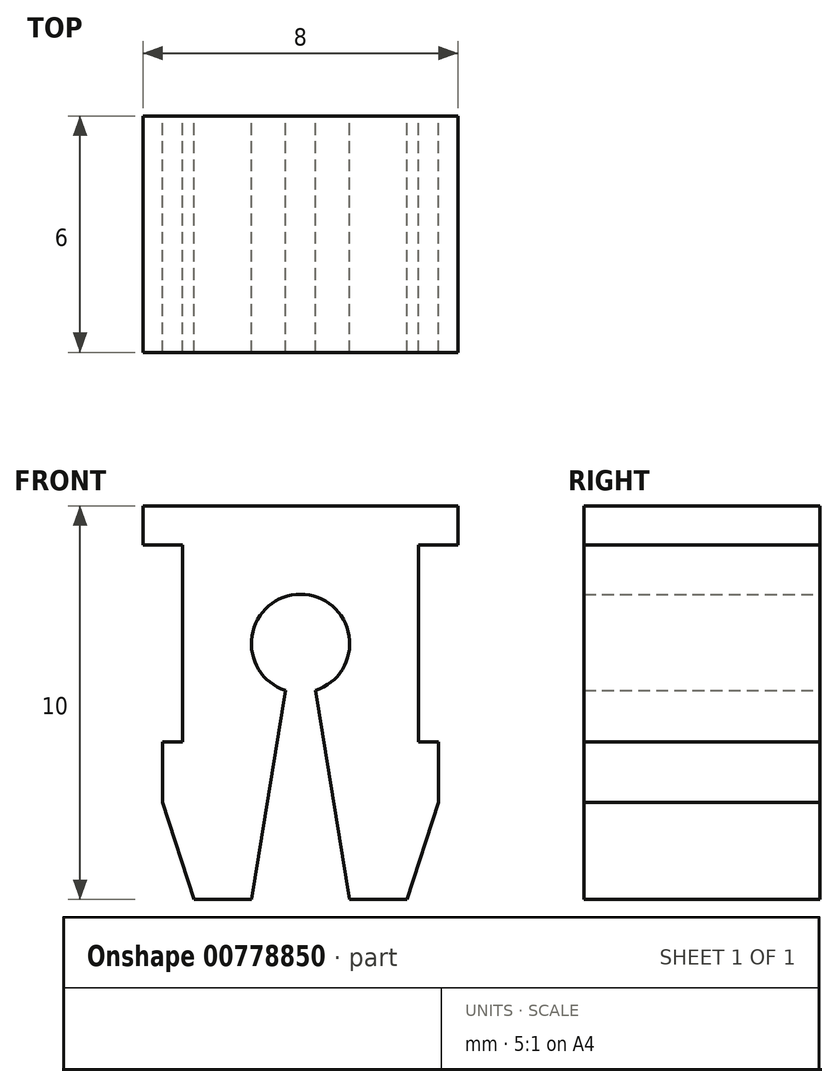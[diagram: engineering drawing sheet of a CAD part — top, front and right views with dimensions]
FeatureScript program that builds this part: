
annotation { "Feature Type Name" : "Feature", "Feature Type Description" : "" }
export const myFeature = defineFeature(function(context is Context, id is Id, definition is map)
    precondition{}
    {
        {
            var Q0;
            Q0=qCreatedBy(makeId("Front.planeOp"),FACE);
            var sketch = newSketch(context, id + "F0", { "sketchPlane" : qUnion([Q0])});
            skLineSegment(sketch, "E0.bottom", {"start": v(-4, 3.5) * mm, "end": v(4, 3.5) * mm});
            skLineSegment(sketch, "E0.top", {"start": v(-4, -6.5) * mm, "end": v(4, -6.5) * mm});
            skLineSegment(sketch, "E0.left", {"start": v(-4, 3.5) * mm, "end": v(-4, -6.5) * mm});
            skLineSegment(sketch, "E0.right", {"start": v(4, 3.5) * mm, "end": v(4, -6.5) * mm});
            skLineSegment(sketch, "E1.bottom", {"start": v(-4, 2.5) * mm, "end": v(-3, 2.5) * mm});
            skLineSegment(sketch, "E1.top", {"start": v(-4, -2.5) * mm, "end": v(-3, -2.5) * mm});
            skLineSegment(sketch, "E1.left", {"start": v(-4, 2.5) * mm, "end": v(-4, -2.5) * mm});
            skLineSegment(sketch, "E1.right", {"start": v(-3, 2.5) * mm, "end": v(-3, -2.5) * mm});
            skLineSegment(sketch, "E2.bottom", {"start": v(4, -2.5) * mm, "end": v(3, -2.5) * mm});
            skLineSegment(sketch, "E2.top", {"start": v(4, 2.5) * mm, "end": v(3, 2.5) * mm});
            skLineSegment(sketch, "E2.left", {"start": v(4, -2.5) * mm, "end": v(4, 2.5) * mm});
            skLineSegment(sketch, "E2.right", {"start": v(3, -2.5) * mm, "end": v(3, 2.5) * mm});
            skCircle(sketch, "E3", {"center": v(0, 0) * mm, "radius": 1.25 * mm});
            skLineSegment(sketch, "E4", {"start": v(-0.38, -1.2) * mm, "end": v(-1.25, -6.5) * mm});
            skLineSegment(sketch, "E5", {"start": v(0.38, -1.2) * mm, "end": v(1.25, -6.5) * mm});
            skLineSegment(sketch, "E6", {"start": v(-3.5, -2.5) * mm, "end": v(-3.5, -6.5) * mm});
            skLineSegment(sketch, "E7", {"start": v(3.5, -2.5) * mm, "end": v(3.5, -6.5) * mm});
            skLineSegment(sketch, "E8", {"start": v(-4, -2.5) * mm, "end": v(-2.7, -6.5) * mm});
            skLineSegment(sketch, "E9", {"start": v(4, -2.5) * mm, "end": v(2.7, -6.5) * mm});
            skSolve(sketch);
        }
        {
            var Q0;
            {var subQ7=sQuery(id+"F0.wireOp",EDGE,"E0.bottom");Q0=makeQuery(id+"F0.imprint","IMPRINT",FACE,{"disambiguationData":[TD([[makeQuery(id+"F0.imprint","IMPRINT",EDGE,{"derivedFrom":subQ7}),-1.0]])]});}
            extrude(context, id + "F1", {"entities" : qUnion([Q0]), "depth" : 6 * mm, "offsetDistance" : 25 * mm});
        }
    });
